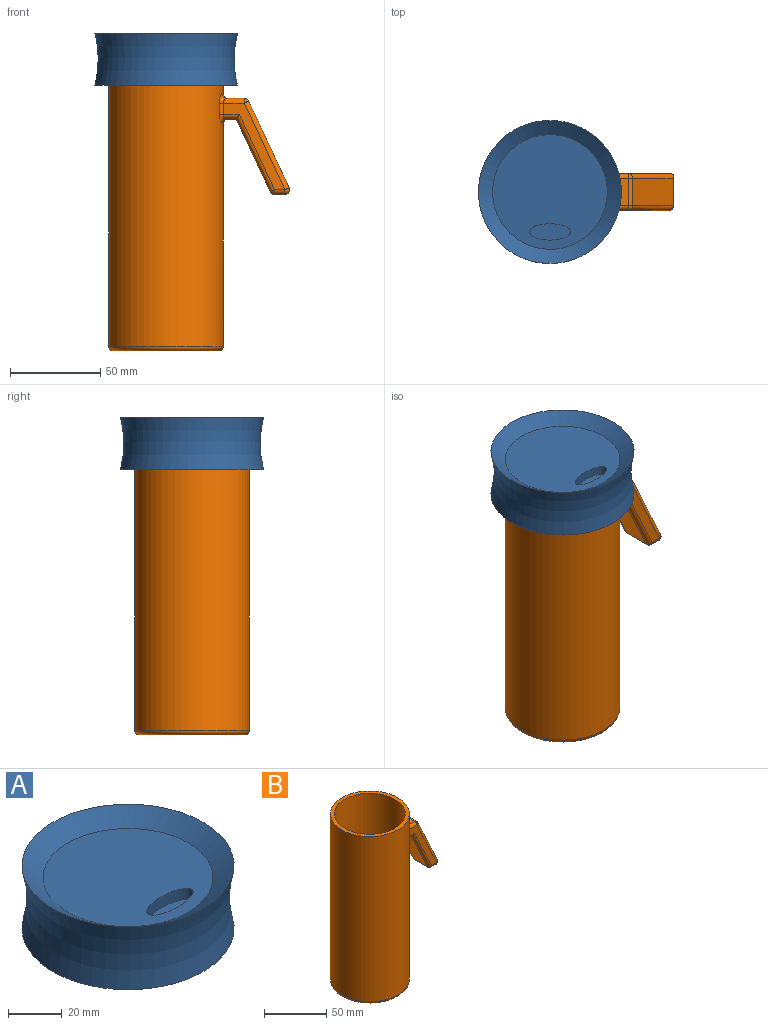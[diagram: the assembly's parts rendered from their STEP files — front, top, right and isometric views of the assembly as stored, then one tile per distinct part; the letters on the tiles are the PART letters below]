
ASSEMBLY  parts=2 mates=1
PART A: 8 faces, bbox 118.9x118.9x83.7 mm
  f0: torus R=96.77mm, axis (0,0,1), area 7019.7mm2, adj f1,f5
  f1: cone r=31.75mm half-angle=54.9deg, axis (0,0,1), area 2151.4mm2, adj f0,f2
  f2: plane 63.5x63.5mm, normal (0,0,1), area 3003.9mm2, adj f1,f6
  f3: plane 63.5x63.5mm, normal (0,0,-1), area 3166.9mm2, adj f4
  f4: cylinder r=31.75mm len=63.5mm, axis (0,0,1), area 3598.1mm2, adj f3,f5
  f5: plane 79.2x79.2mm, normal (0,0,-1), area 1760.1mm2, adj f0,f4
  f6: extruded ~22.78x9.11mm, area 266.3mm2, adj f2,f7
  f7: plane 22.78x9.11mm, normal (0,0,1), area 163mm2, adj f6
PART B: 36 faces, bbox 103.6x68.7x165.1 mm
  f0: cylinder r=31.75mm len=162.56mm, axis (0,0,-1), area 32053.3mm2, adj f2,f21,f25,f26,f29,f30,f32,f33
  f1: cylinder r=28.57mm len=165.1mm, axis (0,0,-1), area 29642.4mm2, adj f2,f3
  f2: plane 63.5x63.5mm, normal (0,0,1), area 601.7mm2, adj f0,f1
  f3: plane 58.42x58.42mm, normal (0,0,-1), area 115.3mm2, adj f1,f35
  f4: plane 48.03x34.01mm, normal (0,-1,0), area 325.9mm2, adj f14,f18,f22,f27,f30,f31
  f5: plane 50.57x35.09mm, normal (0,1,0), area 340.6mm2, adj f7,f11,f12,f20,f24,f28,f29
  f6: plane 40.21x18.75mm, normal (-0.91,0,-0.42), area 676.2mm2, adj f10,f19,f24,f27
  f7: plane 17.79x5.84mm, normal (0,0,-1), area 103.5mm2, adj f5,f11,f18,f19,f24
  f8: plane 48.03x22.4mm, normal (0.91,0,0.42), area 807.6mm2, adj f11,f12,f13,f14
  f9: plane 15.24x10.03mm, normal (0,0,1), area 144.2mm2, adj f13,f20,f21,f22
  f10: plane 15.24x5.55mm, normal (0,0,-1), area 75.9mm2, adj f6,f28,f31,f34
  f11: cylinder r=2.54mm len=17.78mm, axis (0,1,0), area 87mm2, adj f5,f7,f8,f12,f15
  f12: cylinder r=2.54mm len=51.4mm, axis (-0.42,0,0.91), area 217.9mm2, adj f5,f8,f11,f16
  f13: cylinder r=2.54mm len=15.24mm, axis (0,1,0), area 43.9mm2, adj f8,f9,f16,f17
  f14: cylinder r=2.54mm len=49.1mm, axis (0.42,0,-0.91), area 211.4mm2, adj f4,f8,f15,f17
  f15: sphere r=2.54mm, area 12.9mm2, adj f11,f14,f18
  f16: sphere r=2.54mm, area 7.3mm2, adj f12,f13,f20
  f17: sphere r=2.54mm, area 7.3mm2, adj f13,f14,f22
  f18: cylinder r=2.54mm len=5.83mm, axis (-1,0,0), area 23.2mm2, adj f4,f7,f15,f23
  f19: cylinder r=2.54mm len=17.54mm, axis (0,1,0), area 47.6mm2, adj f6,f7,f23,f24
  f20: cylinder r=2.54mm len=11.62mm, axis (-1,0,0), area 43.8mm2, adj f5,f9,f16,f25
  f21: torus R=34.29mm, axis (0,0,1), area 58.4mm2, adj f0,f9,f25,f26
  f22: cylinder r=2.54mm len=11.62mm, axis (1,0,0), area 43.8mm2, adj f4,f9,f17,f26
  f23: sphere r=2.54mm, area 7.3mm2, adj f18,f19,f27
  f24: cylinder r=2.54mm len=45.29mm, axis (0.42,0,-0.91), area 185.9mm2, adj f5,f6,f7,f19,f28
  f25: bspline ~6.09x5.76mm, area 19.4mm2, adj f0,f20,f21,f29
  f26: bspline ~6.15x5.36mm, area 19.4mm2, adj f0,f21,f22,f30
  f27: cylinder r=2.54mm len=42.75mm, axis (-0.42,0,0.91), area 179.4mm2, adj f4,f6,f23,f31
  f28: cylinder r=2.54mm len=8.75mm, axis (1,0,0), area 28.3mm2, adj f5,f10,f24,f32
  f29: cylinder r=2.54mm len=6.35mm, axis (0,0,-1), area 19.2mm2, adj f0,f5,f25,f32
  f30: cylinder r=2.54mm len=6.35mm, axis (0,0,-1), area 19.2mm2, adj f0,f4,f26,f33
  f31: cylinder r=2.54mm len=8.75mm, axis (-1,0,0), area 28.3mm2, adj f4,f10,f27,f33
  f32: bspline ~6.15x5.36mm, area 19.4mm2, adj f0,f28,f29,f34
  f33: bspline ~6.09x5.76mm, area 19.4mm2, adj f0,f30,f31,f34
  f34: torus R=34.29mm, axis (0,0,-1), area 58.4mm2, adj f0,f10,f32,f33
  f35: torus R=29.21mm, axis (0,0,1), area 772.8mm2, adj f0,f3
PLACE A t=(-3.32,0.51,66.55)mm
PLACE B t=(-3.32,0.51,-12.23)mm
MATE revolute A.f4 <-> B.f0  axis (0,0,-1) through (-3.32,0.51,70.32)mm
